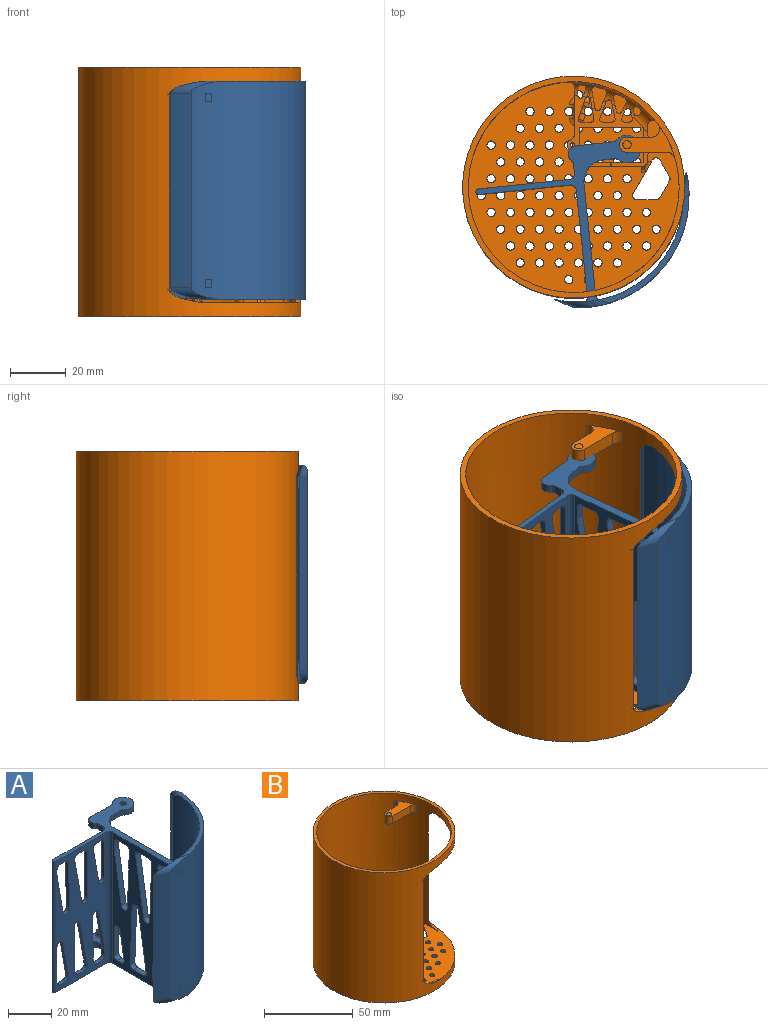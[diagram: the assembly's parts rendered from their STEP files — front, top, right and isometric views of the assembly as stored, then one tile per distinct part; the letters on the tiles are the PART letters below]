
ASSEMBLY  parts=2 mates=1
PART A: 156 faces, bbox 83.3x64.7x78.8 mm
  f0: plane 74x38.02mm, normal (0,1,0), area 1722.9mm2, adj f2,f21,f48,f49,f51,f52,f95,f96
  f1: plane 74x33.02mm, normal (0,-1,0), area 1444.8mm2, adj f21,f48,f95,f96,f97,f98,f99,f100
  f2: plane 71.03x47.74mm, normal (1,0,0), area 1771.1mm2, adj f0,f5,f8,f11,f21,f27,f31,f32
  f3: plane 1.92x1.73mm, normal (0,0,-1), area 0.7mm2, adj f4,f6,f7,f50
  f4: plane 74.05x38.91mm, normal (-1,0,0), area 1618.2mm2, adj f3,f6,f21,f26,f47,f49,f55,f56
  f5: cylinder r=1.5mm len=5.96mm, axis (0,0,-1), area 12.6mm2, adj f2,f7,f50,f140
  f6: cylinder r=1.5mm len=8.91mm, axis (0,0,-1), area 19.4mm2, adj f3,f4,f7,f140
  f7: cylinder r=38mm len=78.8mm, axis (0,0,-1), area 5694.5mm2, adj f3,f5,f6,f13,f14,f15,f16,f17
  f8: plane 26.14x16mm, normal (0,0,-1), area 184.2mm2, adj f2,f9,f33,f34,f35,f36,f37,f38
  f9: plane 4x3.44mm, normal (-1,0,0), area 11.3mm2, adj f8,f32,f38,f52,f135
  f10: plane 4x3.44mm, normal (-1,0,0), area 11.3mm2, adj f11,f21,f29,f51,f137
  f11: plane 26.14x16mm, normal (0,0,-1), area 161.7mm2, adj f2,f10,f22,f23,f24,f25,f28,f29
  f12: cylinder r=40mm len=78.8mm, axis (0,0,-1), area 5675.7mm2, adj f13,f14,f15,f16,f17,f18,f19,f20
  f13: cylinder r=60.11mm len=70mm, axis (0,0,-1), area 551.9mm2, adj f7,f12,f17,f20
  f14: cylinder r=23.1mm len=70mm, axis (0,0,-1), area 236.9mm2, adj f7,f12,f16,f19
  f15: plane 37.31x36.38mm, normal (0,0,-1), area 104mm2, adj f7,f12,f16,f17
  f16: torus R=27.5mm, axis (0,0,-1), area 22.4mm2, adj f7,f12,f14,f15
  f17: torus R=55.71mm, axis (0,0,-1), area 45.8mm2, adj f7,f12,f13,f15
  f18: plane 37.31x36.38mm, normal (0,0,1), area 104mm2, adj f7,f12,f19,f20
  f19: torus R=27.5mm, axis (0,0,1), area 22.4mm2, adj f7,f12,f14,f18
  f20: torus R=55.71mm, axis (0,0,1), area 45.8mm2, adj f7,f12,f13,f18
  f21: plane 60.67x56.26mm, normal (0,0,1), area 398.5mm2, adj f0,f1,f2,f4,f10,f22,f23,f24
  f22: cylinder r=3mm len=5.24mm, axis (0,0,1), area 21.7mm2, adj f11,f21,f25,f29
  f23: plane 3.95x3mm, normal (0,-1,0), area 11.9mm2, adj f11,f21,f30,f31
  f24: cylinder r=5mm len=10mm, axis (0,0,1), area 71.3mm2, adj f11,f21,f28,f30
  f25: plane 13.45x3mm, normal (0,1,0), area 40.4mm2, adj f11,f21,f22,f28
  f26: cylinder r=1.5mm len=6.95mm, axis (0,0,-1), area 12.2mm2, adj f4,f7,f139,f141
  f27: cylinder r=1.5mm len=6.97mm, axis (0,0,-1), area 12.6mm2, adj f2,f7,f139,f141
  f28: cylinder r=1.5mm len=3mm, axis (0,0,1), area 3.6mm2, adj f11,f21,f24,f25
  f29: cylinder r=1.5mm len=3mm, axis (0,0,1), area 3.8mm2, adj f10,f11,f21,f22
  f30: cylinder r=1.5mm len=3mm, axis (0,0,1), area 3.6mm2, adj f11,f21,f23,f24
  f31: cylinder r=8mm len=8mm, axis (0,0,-1), area 37.7mm2, adj f2,f11,f21,f23
  f32: plane 26.14x16mm, normal (0,0,1), area 148.9mm2, adj f2,f9,f33,f34,f35,f36,f37,f38
  f33: cylinder r=3mm len=5.24mm, axis (0,0,-1), area 21.7mm2, adj f8,f32,f34,f38
  f34: plane 13.45x3mm, normal (0,1,0), area 40.4mm2, adj f8,f32,f33,f37
  f35: cylinder r=5mm len=10mm, axis (0,0,-1), area 71.3mm2, adj f8,f32,f37,f39
  f36: plane 3.95x3mm, normal (0,-1,0), area 11.9mm2, adj f8,f32,f39,f40
  f37: cylinder r=1.5mm len=3mm, axis (0,0,-1), area 3.6mm2, adj f8,f32,f34,f35
  f38: cylinder r=1.5mm len=3mm, axis (0,0,-1), area 3.8mm2, adj f8,f9,f32,f33
  f39: cylinder r=1.5mm len=3mm, axis (0,0,-1), area 3.6mm2, adj f8,f32,f35,f36
  f40: cylinder r=8mm len=8mm, axis (0,0,1), area 37.7mm2, adj f2,f8,f32,f36
  f41: cylinder r=1.5mm len=3mm, axis (0,0,-1), area 6.6mm2, adj f21,f42
  f42: plane 6x6mm, normal (0,0,-1), area 21.2mm2, adj f41,f43
  f43: cylinder r=3mm len=6mm, axis (0,0,-1), area 43.4mm2, adj f11,f42
  f44: cylinder r=1.5mm len=3mm, axis (0,0,1), area 6.6mm2, adj f8,f45
  f45: plane 6x6mm, normal (0,0,1), area 21.2mm2, adj f44,f46
  f46: cylinder r=3mm len=6mm, axis (0,0,1), area 43.4mm2, adj f32,f45
  f47: plane 62.05x3mm, normal (0.06,-1,0), area 186.4mm2, adj f2,f4,f139,f140
  f48: plane 36.02x4mm, normal (0,0,-1), area 72.5mm2, adj f0,f1,f49,f138,f155
  f49: cylinder r=3mm len=43mm, axis (0,1,0), area 201.5mm2, adj f0,f2,f4,f48,f50,f60,f66,f74
  f50: torus R=4.5mm, axis (0,0,-1), area 11.1mm2, adj f3,f5,f7,f49
  f51: cylinder r=5mm len=5mm, axis (1,0,0), area 28.2mm2, adj f0,f2,f10,f11,f137
  f52: cylinder r=5mm len=5mm, axis (1,0,0), area 28.2mm2, adj f0,f2,f9,f32,f135
  f53: cylinder r=40mm len=3mm, axis (0,0,-1), area 6.8mm2, adj f12
  f54: cylinder r=40mm len=3mm, axis (0,0,-1), area 6.8mm2, adj f12
  f55: plane 33.19x5.29mm, normal (0,0.99,-0.16), area 100.8mm2, adj f2,f4,f57,f58
  f56: plane 33.19x3mm, normal (0,-1,-0.04), area 99.6mm2, adj f2,f4,f57,f59
  f57: cylinder r=2mm len=3.97mm, axis (1,0,0), area 17.7mm2, adj f2,f4,f55,f56
  f58: cylinder r=2mm len=3mm, axis (1,0,0), area 10.4mm2, adj f2,f4,f55,f60
  f59: cylinder r=2mm len=3mm, axis (-1,0,0), area 9.6mm2, adj f2,f4,f56,f60
  f60: plane 6.53x3mm, normal (0,0,1), area 19.6mm2, adj f4,f49,f58,f59
  f61: plane 15.36x3mm, normal (0,0.99,-0.16), area 46.7mm2, adj f2,f4,f63,f64
  f62: plane 15.36x3mm, normal (0,-1,0), area 46.1mm2, adj f2,f4,f63,f65
  f63: cylinder r=2mm len=3.98mm, axis (-1,0,0), area 17.9mm2, adj f2,f4,f61,f62
  f64: cylinder r=2mm len=3mm, axis (1,0,0), area 10.4mm2, adj f2,f4,f61,f66
  f65: cylinder r=2mm len=3mm, axis (-1,0,0), area 9.4mm2, adj f2,f4,f62,f66
  f66: plane 3x2.45mm, normal (0,0,1), area 7.3mm2, adj f4,f49,f64,f65
  f67: plane 4.14x3mm, normal (0,1,0), area 12.4mm2, adj f2,f4,f70,f73
  f68: plane 29.05x4.63mm, normal (0,0.99,-0.16), area 88.3mm2, adj f2,f4,f70,f71
  f69: plane 33.19x3mm, normal (0,-1,-0.04), area 99.6mm2, adj f2,f4,f71,f72
  f70: cylinder r=2mm len=3mm, axis (1,0,0), area 0.9mm2, adj f2,f4,f67,f68
  f71: cylinder r=2mm len=3.97mm, axis (1,0,0), area 17.7mm2, adj f2,f4,f68,f69
  f72: cylinder r=2mm len=3mm, axis (-1,0,0), area 9.6mm2, adj f2,f4,f69,f74
  f73: cylinder r=2mm len=3mm, axis (1,0,0), area 9.4mm2, adj f2,f4,f67,f74
  f74: plane 5.87x3mm, normal (0,0,1), area 17.6mm2, adj f4,f49,f72,f73
  f75: plane 15.36x3mm, normal (0,-0.99,0.16), area 46.7mm2, adj f2,f4,f78,f79
  f76: plane 3x2.45mm, normal (0,0,-1), area 7.3mm2, adj f2,f4,f79,f80
  f77: plane 15.36x3mm, normal (0,1,0), area 46.1mm2, adj f2,f4,f78,f80
  f78: cylinder r=2mm len=3.98mm, axis (-1,0,0), area 17.9mm2, adj f2,f4,f75,f77
  f79: cylinder r=2mm len=3mm, axis (1,0,0), area 10.4mm2, adj f2,f4,f75,f76
  f80: cylinder r=2mm len=3mm, axis (-1,0,0), area 9.4mm2, adj f2,f4,f76,f77
  f81: plane 33.19x5.29mm, normal (0,-0.99,0.16), area 100.8mm2, adj f2,f4,f84,f86
  f82: plane 33.19x3mm, normal (0,1,0.04), area 99.6mm2, adj f2,f4,f85,f86
  f83: plane 6.53x3mm, normal (0,0,-1), area 19.6mm2, adj f2,f4,f84,f85
  f84: cylinder r=2mm len=3mm, axis (1,0,0), area 10.4mm2, adj f2,f4,f81,f83
  f85: cylinder r=2mm len=3mm, axis (-1,0,0), area 9.6mm2, adj f2,f4,f82,f83
  f86: cylinder r=2mm len=3.97mm, axis (1,0,0), area 17.7mm2, adj f2,f4,f81,f82
  f87: plane 29.05x4.63mm, normal (0,-0.99,0.16), area 88.3mm2, adj f2,f4,f91,f94
  f88: plane 33.19x3mm, normal (0,1,0.04), area 99.6mm2, adj f2,f4,f92,f94
  f89: plane 5.87x3mm, normal (0,0,-1), area 17.6mm2, adj f2,f4,f92,f93
  f90: plane 4.14x3mm, normal (0,-1,0), area 12.4mm2, adj f2,f4,f91,f93
  f91: cylinder r=2mm len=3mm, axis (1,0,0), area 0.9mm2, adj f2,f4,f87,f90
  f92: cylinder r=2mm len=3mm, axis (-1,0,0), area 9.6mm2, adj f2,f4,f88,f89
  f93: cylinder r=2mm len=3mm, axis (1,0,0), area 9.4mm2, adj f2,f4,f89,f90
  f94: cylinder r=2mm len=3.97mm, axis (1,0,0), area 17.7mm2, adj f2,f4,f87,f88
  f95: plane 25.99x4.58mm, normal (-0.98,0,-0.17), area 52.8mm2, adj f0,f1,f98,f100
  f96: plane 25.99x2mm, normal (1,0,0.01), area 52mm2, adj f0,f1,f99,f100
  f97: plane 4.26x2mm, normal (0,0,1), area 8.5mm2, adj f0,f1,f98,f99
  f98: cylinder r=2mm len=2.35mm, axis (0,1,0), area 7mm2, adj f0,f1,f95,f97
  f99: cylinder r=2mm len=2mm, axis (0,-1,0), area 6.2mm2, adj f0,f1,f96,f97
  f100: cylinder r=2mm len=3.97mm, axis (0,1,0), area 11.9mm2, adj f0,f1,f95,f96
  f101: plane 20.47x3.61mm, normal (0.98,0,0.17), area 41.6mm2, adj f0,f1,f104,f105
  f102: plane 3.61x2mm, normal (0,0,-1), area 7.2mm2, adj f0,f1,f105,f106
  f103: plane 20.46x2mm, normal (-1,0,0), area 40.9mm2, adj f0,f1,f104,f106
  f104: cylinder r=2mm len=3.97mm, axis (0,-1,0), area 11.9mm2, adj f0,f1,f101,f103
  f105: cylinder r=2mm len=2.35mm, axis (0,1,0), area 7mm2, adj f0,f1,f101,f102
  f106: cylinder r=2mm len=2mm, axis (0,-1,0), area 6.3mm2, adj f0,f1,f102,f103
  f107: plane 25.99x4.58mm, normal (0.98,0,0.17), area 52.8mm2, adj f0,f1,f110,f112
  f108: plane 25.99x2mm, normal (-1,0,-0.01), area 52mm2, adj f0,f1,f111,f112
  f109: plane 4.26x2mm, normal (0,0,-1), area 8.5mm2, adj f0,f1,f110,f111
  f110: cylinder r=2mm len=2.35mm, axis (0,1,0), area 7mm2, adj f0,f1,f107,f109
  f111: cylinder r=2mm len=2mm, axis (0,-1,0), area 6.2mm2, adj f0,f1,f108,f109
  f112: cylinder r=2mm len=3.97mm, axis (0,1,0), area 11.9mm2, adj f0,f1,f107,f108
  f113: plane 20.47x3.61mm, normal (-0.98,0,-0.17), area 41.6mm2, adj f0,f1,f116,f117
  f114: plane 3.61x2mm, normal (0,0,1), area 7.2mm2, adj f0,f1,f117,f118
  f115: plane 20.46x2mm, normal (1,0,0), area 40.9mm2, adj f0,f1,f116,f118
  f116: cylinder r=2mm len=3.97mm, axis (0,-1,0), area 11.9mm2, adj f0,f1,f113,f115
  f117: cylinder r=2mm len=2.35mm, axis (0,1,0), area 7mm2, adj f0,f1,f113,f114
  f118: cylinder r=2mm len=2mm, axis (0,1,0), area 6.3mm2, adj f0,f1,f114,f115
  f119: plane 25.99x2mm, normal (-1,0,-0.01), area 52mm2, adj f0,f1,f124,f126
  f120: plane 22.78x4.02mm, normal (0.98,0,0.17), area 46.3mm2, adj f0,f1,f123,f126
  f121: plane 3.7x2mm, normal (0,0,-1), area 7.4mm2, adj f0,f1,f124,f125
  f122: plane 3.21x2mm, normal (1,0,0), area 6.4mm2, adj f0,f1,f123,f125
  f123: cylinder r=2mm len=2mm, axis (0,1,0), area 0.7mm2, adj f0,f1,f120,f122
  f124: cylinder r=2mm len=2mm, axis (0,-1,0), area 6.2mm2, adj f0,f1,f119,f121
  f125: cylinder r=2mm len=2mm, axis (0,-1,0), area 6.3mm2, adj f0,f1,f121,f122
  f126: cylinder r=2mm len=3.97mm, axis (0,1,0), area 11.9mm2, adj f0,f1,f119,f120
  f127: plane 3.7x2mm, normal (0,0,1), area 7.4mm2, adj f0,f1,f131,f133
  f128: plane 3.21x2mm, normal (-1,0,0), area 6.4mm2, adj f0,f1,f132,f133
  f129: plane 22.78x4.02mm, normal (-0.98,0,-0.17), area 46.3mm2, adj f0,f1,f132,f134
  f130: plane 25.99x2mm, normal (1,0,0.01), area 52mm2, adj f0,f1,f131,f134
  f131: cylinder r=2mm len=2mm, axis (0,-1,0), area 6.2mm2, adj f0,f1,f127,f130
  f132: cylinder r=2mm len=2mm, axis (0,1,0), area 0.7mm2, adj f0,f1,f128,f129
  f133: cylinder r=2mm len=2mm, axis (0,1,0), area 6.3mm2, adj f0,f1,f127,f128
  f134: cylinder r=2mm len=3.97mm, axis (0,1,0), area 11.9mm2, adj f0,f1,f129,f130
  f135: cylinder r=2mm len=10mm, axis (0,0,-1), area 22mm2, adj f0,f9,f52,f136
  f136: cylinder r=2mm len=5mm, axis (-1,0,0), area 12.5mm2, adj f0,f2,f8,f49,f135
  f137: cylinder r=2mm len=8mm, axis (0,0,-1), area 18.8mm2, adj f0,f10,f21,f51
  f138: cylinder r=2mm len=74mm, axis (0,0,1), area 232.5mm2, adj f1,f4,f21,f48
  f139: bspline ~6.4x1.97mm, area 12.7mm2, adj f7,f26,f27,f47
  f140: bspline ~6.25x1.97mm, area 12.7mm2, adj f5,f6,f7,f47
  f141: torus R=36mm, axis (0,0,1), area 12.8mm2, adj f2,f4,f7,f21,f26,f27
  f142: cylinder r=0.7mm len=3mm, axis (0,0,1), area 13.2mm2, adj f8,f32
  f143: cylinder r=0.7mm len=3mm, axis (0,0,1), area 13.2mm2, adj f8,f32
  f144: cylinder r=0.7mm len=3mm, axis (0,0,1), area 13.2mm2, adj f8,f32
  f145: cylinder r=0.7mm len=3mm, axis (0,0,1), area 13.2mm2, adj f8,f32
  f146: cylinder r=0.7mm len=3mm, axis (0,0,1), area 13.2mm2, adj f8,f32
  f147: cylinder r=2.28mm len=4.54mm, axis (0,0,-1), area 9.9mm2, adj f148,f150,f151,f152,f153,f154
  f148: plane 1.5x0.7mm, normal (1,-0.08,0), area 0.4mm2, adj f32,f147,f149,f152,f153
  f149: cylinder r=2.08mm len=4.15mm, axis (0,0,-1), area 12.1mm2, adj f32,f148,f150,f151,f153,f154
  f150: plane 1.5x0.7mm, normal (1,0.08,0), area 0.4mm2, adj f32,f147,f149,f152,f154
  f151: plane 4.35x1.61mm, normal (0,0,1), area 1.1mm2, adj f147,f149,f153,f154
  f152: torus R=2.78mm, axis (0,0,-1), area 5.8mm2, adj f32,f147,f148,f150
  f153: cylinder r=0.5mm len=0.52mm, axis (-0.08,-1,0), area 0.2mm2, adj f147,f148,f149,f151
  f154: cylinder r=0.5mm len=0.52mm, axis (0.08,-1,0), area 0.2mm2, adj f147,f149,f150,f151
  f155: cylinder r=1mm len=74mm, axis (0,0,-1), area 232.5mm2, adj f0,f1,f21,f48
PART B: 219 faces, bbox 89.8x86x90.2 mm
  f0: bspline ~2x1.98mm, area 1.2mm2, adj f66,f197,f203,f205
  f1: plane 4.54x3.28mm, normal (0,0,-1), area 5.9mm2, adj f118,f133,f136,f162,f166,f179,f195,f196
  f2: plane 8.23x1.5mm, normal (0,0,-1), area 12.3mm2, adj f5,f6,f187,f200
  f3: plane 76x76mm, normal (0,0,-1), area 3835.2mm2, adj f8,f9,f10,f11,f12,f13,f14,f15
  f4: plane 31.67x25.08mm, normal (0,0,-1), area 152.4mm2, adj f118,f119,f120,f121,f123,f124,f125,f126
  f5: plane 10.93x6.7mm, normal (0,-1,0), area 45.3mm2, adj f2,f7,f131,f187,f200
  f6: plane 20.8x11.43mm, normal (0,1,0), area 55.7mm2, adj f2,f7,f99,f126,f187,f194,f200
  f7: plane 31.67x25.53mm, normal (0,0,1), area 196.3mm2, adj f5,f6,f118,f119,f120,f121,f122,f123
  f8: cylinder r=1.5mm len=3mm, axis (0,0,-1), area 9.4mm2, adj f3,f99
  f9: cylinder r=1.5mm len=3mm, axis (0,0,-1), area 9.4mm2, adj f3,f99
  f10: cylinder r=1.5mm len=3mm, axis (0,0,-1), area 9.4mm2, adj f3,f99
  f11: cylinder r=1.5mm len=3mm, axis (0,0,-1), area 9.4mm2, adj f3,f99
  f12: cylinder r=1.5mm len=3mm, axis (0,0,-1), area 9.4mm2, adj f3,f99
  f13: cylinder r=1.5mm len=3mm, axis (0,0,-1), area 9.4mm2, adj f3,f99
  f14: cylinder r=1.5mm len=3mm, axis (0,0,-1), area 9.4mm2, adj f3,f99
  f15: cylinder r=1.5mm len=3mm, axis (0,0,-1), area 9.4mm2, adj f3,f99
  f16: cylinder r=1.5mm len=3mm, axis (0,0,-1), area 9.4mm2, adj f3,f99
  f17: cylinder r=1.5mm len=3mm, axis (0,0,-1), area 9.4mm2, adj f3,f99
  f18: cylinder r=1.5mm len=3mm, axis (0,0,-1), area 9.4mm2, adj f3,f99
  f19: cylinder r=1.5mm len=3mm, axis (0,0,-1), area 9.4mm2, adj f3,f99
  f20: cylinder r=1.5mm len=3mm, axis (0,0,-1), area 9.4mm2, adj f3,f99
  f21: cylinder r=1.5mm len=3mm, axis (0,0,-1), area 9.4mm2, adj f3,f99
  f22: cylinder r=1.5mm len=3mm, axis (0,0,-1), area 9.4mm2, adj f3,f99
  f23: cylinder r=1.5mm len=3mm, axis (0,0,-1), area 9.4mm2, adj f3,f99
  f24: cylinder r=1.5mm len=3mm, axis (0,0,-1), area 9.4mm2, adj f3,f99
  f25: cylinder r=1.5mm len=3mm, axis (0,0,-1), area 9.4mm2, adj f3,f99
  f26: cylinder r=1.5mm len=3mm, axis (0,0,-1), area 9.4mm2, adj f3,f99
  f27: cylinder r=1.5mm len=3mm, axis (0,0,-1), area 9.4mm2, adj f3,f99
  f28: cylinder r=1.5mm len=3mm, axis (0,0,-1), area 9.4mm2, adj f3,f99
  f29: cylinder r=1.5mm len=3mm, axis (0,0,-1), area 9.4mm2, adj f3,f99
  f30: cylinder r=1.5mm len=3mm, axis (0,0,-1), area 9.4mm2, adj f3,f99
  f31: cylinder r=1.5mm len=3mm, axis (0,0,-1), area 9.4mm2, adj f3,f99
  f32: cylinder r=1.5mm len=3mm, axis (0,0,-1), area 9.4mm2, adj f3,f99
  f33: cylinder r=1.5mm len=3mm, axis (0,0,-1), area 9.4mm2, adj f3,f99
  f34: cylinder r=1.5mm len=3mm, axis (0,0,-1), area 9.4mm2, adj f3,f99
  f35: cylinder r=1.5mm len=3mm, axis (0,0,-1), area 9.4mm2, adj f3,f99
  f36: cylinder r=1.5mm len=3mm, axis (0,0,-1), area 9.4mm2, adj f3,f99
  f37: cylinder r=1.5mm len=3mm, axis (0,0,-1), area 9.4mm2, adj f3,f99
  f38: cylinder r=1.5mm len=3mm, axis (0,0,-1), area 9.4mm2, adj f3,f99
  f39: cylinder r=1.5mm len=3mm, axis (0,0,-1), area 9.4mm2, adj f3,f99
  f40: cylinder r=1.5mm len=3mm, axis (0,0,-1), area 9.4mm2, adj f3,f99
  f41: cylinder r=1.5mm len=3mm, axis (0,0,-1), area 9.4mm2, adj f3,f99
  f42: cylinder r=1.5mm len=3mm, axis (0,0,-1), area 9.4mm2, adj f3,f99
  f43: cylinder r=1.5mm len=3mm, axis (0,0,-1), area 9.4mm2, adj f3,f99
  f44: cylinder r=1.5mm len=3mm, axis (0,0,-1), area 9.4mm2, adj f3,f99
  f45: cylinder r=1.5mm len=3mm, axis (0,0,-1), area 9.4mm2, adj f3,f99
  f46: cylinder r=1.5mm len=3mm, axis (0,0,-1), area 9.4mm2, adj f3,f99
  f47: cylinder r=1.5mm len=3mm, axis (0,0,-1), area 9.4mm2, adj f3,f99
  f48: cylinder r=1.5mm len=3mm, axis (0,0,-1), area 9.4mm2, adj f3,f99
  f49: cylinder r=1.5mm len=3mm, axis (0,0,-1), area 9.4mm2, adj f3,f99
  f50: cylinder r=1.5mm len=3mm, axis (0,0,-1), area 9.4mm2, adj f3,f99
  f51: cylinder r=1.5mm len=3mm, axis (0,0,-1), area 9.4mm2, adj f3,f99
  f52: cylinder r=1.5mm len=3mm, axis (0,0,-1), area 9.4mm2, adj f3,f99
  f53: cylinder r=1.5mm len=3mm, axis (0,0,-1), area 9.4mm2, adj f3,f99
  f54: cylinder r=1.5mm len=3mm, axis (0,0,-1), area 9.4mm2, adj f3,f99
  f55: cylinder r=1.5mm len=3mm, axis (0,0,-1), area 9.4mm2, adj f3,f99
  f56: cylinder r=1.5mm len=3mm, axis (0,0,-1), area 9.4mm2, adj f3,f99
  f57: cylinder r=1.5mm len=3mm, axis (0,0,-1), area 9.4mm2, adj f3,f99
  f58: cylinder r=1.5mm len=3mm, axis (0,0,-1), area 9.4mm2, adj f3,f99
  f59: cylinder r=1.5mm len=3mm, axis (0,0,-1), area 9.4mm2, adj f3,f99
  f60: cylinder r=1.5mm len=3mm, axis (0,0,-1), area 9.4mm2, adj f3,f99
  f61: cylinder r=1.5mm len=3mm, axis (0,0,-1), area 9.4mm2, adj f3,f99
  f62: cylinder r=1.5mm len=3mm, axis (0,0,-1), area 9.4mm2, adj f3,f99
  f63: cylinder r=1.5mm len=3mm, axis (0,0,-1), area 9.4mm2, adj f3,f99
  f64: cylinder r=1.5mm len=3mm, axis (0,0,-1), area 9.4mm2, adj f3,f99
  f65: cylinder r=1.5mm len=3mm, axis (0,0,-1), area 9.4mm2, adj f3,f99,f209
  f66: cylinder r=1.5mm len=3mm, axis (0,0,-1), area 9.4mm2, adj f0,f3,f99,f203
  f67: cylinder r=1.5mm len=3mm, axis (0,0,-1), area 9.4mm2, adj f3,f99
  f68: cylinder r=1.5mm len=3mm, axis (0,0,-1), area 9.4mm2, adj f3,f99
  f69: cylinder r=1.5mm len=3mm, axis (0,0,-1), area 9.4mm2, adj f3,f99
  f70: cylinder r=1.5mm len=3mm, axis (0,0,-1), area 9.4mm2, adj f3,f99
  f71: cylinder r=1.5mm len=3mm, axis (0,0,-1), area 9.4mm2, adj f3,f99
  f72: cylinder r=1.5mm len=3mm, axis (0,0,-1), area 9.4mm2, adj f3,f99
  f73: cylinder r=1.5mm len=3mm, axis (0,0,-1), area 9.4mm2, adj f3,f99
  f74: cylinder r=1.5mm len=3mm, axis (0,0,-1), area 10.1mm2, adj f3,f99,f208,f210
  f75: cylinder r=1.5mm len=3mm, axis (0,0,-1), area 9.4mm2, adj f3,f99,f204
  f76: cylinder r=1.5mm len=3mm, axis (0,0,-1), area 9.4mm2, adj f3,f99
  f77: cylinder r=1.5mm len=3mm, axis (0,0,-1), area 9.4mm2, adj f3,f99
  f78: cylinder r=1.5mm len=3mm, axis (0,0,-1), area 9.4mm2, adj f3,f99
  f79: cylinder r=1.5mm len=3mm, axis (0,0,-1), area 9.4mm2, adj f3,f99
  f80: cylinder r=1.5mm len=2.25mm, axis (0,0,-1), area 3.1mm2, adj f3,f99,f191,f192
  f81: cylinder r=1.5mm len=3mm, axis (0,0,-1), area 9.4mm2, adj f3,f99
  f82: cylinder r=1.5mm len=3mm, axis (0,0,-1), area 9.4mm2, adj f3,f99
  f83: cylinder r=1.5mm len=3mm, axis (0,0,-1), area 9.4mm2, adj f3,f99
  f84: cylinder r=1.5mm len=3mm, axis (0,0,-1), area 9.4mm2, adj f3,f99
  f85: cylinder r=1.5mm len=3mm, axis (0,0,-1), area 9.4mm2, adj f3,f99
  f86: cylinder r=1.5mm len=1.3mm, axis (0,0,-1), area 1.6mm2, adj f3,f99,f190,f191
  f87: cylinder r=1.5mm len=3mm, axis (0,0,-1), area 9.4mm2, adj f3,f99
  f88: cylinder r=1.5mm len=3mm, axis (0,0,-1), area 9.4mm2, adj f3,f99
  f89: cylinder r=1.5mm len=6mm, axis (0,0,-1), area 56.5mm2, adj f3,f106
  f90: cylinder r=1.5mm len=2.6mm, axis (0,0,-1), area 3.1mm2, adj f3,f99,f189,f192
  f91: cylinder r=1.5mm len=1.5mm, axis (0,0,-1), area 1.6mm2, adj f3,f99,f189,f190
  f92: cylinder r=38mm len=76mm, axis (0,0,-1), area 955mm2, adj f3,f96
  f93: cylinder r=38mm len=17.49mm, axis (0,0,-1), area 44.8mm2, adj f94,f99,f101
  f94: cylinder r=38mm len=85mm, axis (0,0,-1), area 13467.1mm2, adj f93,f97,f98,f99,f100,f106,f107,f108
  f95: cylinder r=40mm len=90mm, axis (0,0,-1), area 16607.6mm2, adj f96,f97,f98,f99,f100,f101,f107,f108
  f96: plane 80x80mm, normal (0,0,-1), area 490.1mm2, adj f92,f95
  f97: cylinder r=60.71mm len=70mm, axis (0,0,-1), area 608.9mm2, adj f94,f95,f101,f110
  f98: cylinder r=22.5mm len=70mm, axis (0,0,-1), area 240.3mm2, adj f94,f95,f100,f109
  f99: plane 77.9x77.25mm, normal (0,0,1), area 3789.4mm2, adj f6,f8,f9,f10,f11,f12,f13,f14
  f100: torus R=27.5mm, axis (0,0,-1), area 27.9mm2, adj f94,f95,f98,f99
  f101: torus R=55.71mm, axis (0,0,-1), area 55.3mm2, adj f93,f95,f97,f99
  f102: plane 14.46x5mm, normal (0,-1,0), area 72.3mm2, adj f99,f103,f106,f218
  f103: cylinder r=2.75mm len=5.5mm, axis (0,0,-1), area 43.2mm2, adj f99,f102,f104,f106
  f104: plane 8.77x5mm, normal (0,1,0), area 43.9mm2, adj f99,f103,f106,f217
  f105: cylinder r=1.5mm len=5.5mm, axis (0,0,-1), area 51.8mm2, adj f106,f188
  f106: plane 20.1x12.49mm, normal (0,0,1), area 91.3mm2, adj f89,f94,f102,f103,f104,f105,f217,f218
  f107: plane 80x80mm, normal (0,0,1), area 490.1mm2, adj f94,f95
  f108: plane 37.31x36.38mm, normal (0,0,-1), area 104mm2, adj f94,f95,f109,f110
  f109: torus R=27.5mm, axis (0,0,1), area 27.9mm2, adj f94,f95,f98,f108
  f110: torus R=55.71mm, axis (0,0,1), area 55.3mm2, adj f94,f95,f97,f108
  f111: plane 14.46x5mm, normal (0,-1,0), area 72.3mm2, adj f112,f115,f116,f216
  f112: cylinder r=2.75mm len=5.5mm, axis (0,0,1), area 43.2mm2, adj f111,f113,f115,f116
  f113: plane 8.77x5mm, normal (0,1,0), area 43.9mm2, adj f112,f115,f116,f215
  f114: cylinder r=1.5mm len=5mm, axis (0,0,1), area 47.1mm2, adj f115,f116
  f115: plane 20.1x12.49mm, normal (0,0,-1), area 98.4mm2, adj f94,f111,f112,f113,f114,f215,f216
  f116: plane 20.1x12.49mm, normal (0,0,1), area 98.4mm2, adj f94,f111,f112,f113,f114,f215,f216
  f117: plane 4.42x2.29mm, normal (1,0,0), area 9.5mm2, adj f129,f174,f177,f183
  f118: plane 20.24x16.2mm, normal (-1,0,0), area 138.7mm2, adj f1,f4,f7,f128,f176,f179,f180,f196
  f119: cylinder r=2mm len=4mm, axis (0,0,-1), area 18mm2, adj f4,f7,f180,f181
  f120: plane 4x1.28mm, normal (-1,0,0), area 5.1mm2, adj f4,f7,f130,f181
  f121: plane 10.93x4mm, normal (0,-1,0), area 43.7mm2, adj f4,f7,f130,f186
  f122: plane 6.7x1.31mm, normal (1,0,0), area 6.6mm2, adj f7,f131,f182,f199
  f123: plane 11.43x4mm, normal (0,1,0), area 45.7mm2, adj f4,f7,f124,f186
  f124: plane 12.59x4mm, normal (1,0,0), area 50.4mm2, adj f4,f7,f123,f125
  f125: plane 23.03x4mm, normal (0,-1,0), area 92.1mm2, adj f4,f7,f124,f126
  f126: plane 20.8x12.59mm, normal (-1,0,0), area 60.3mm2, adj f4,f6,f7,f99,f125,f193,f199
  f127: cylinder r=2mm len=4mm, axis (0,0,-1), area 17.8mm2, adj f4,f7,f182,f183
  f128: cylinder r=2mm len=14mm, axis (0,0,-1), area 32.2mm2, adj f94,f118,f176,f179
  f129: cylinder r=2mm len=14mm, axis (0,0,-1), area 45.7mm2, adj f94,f117,f174,f177
  f130: cylinder r=2mm len=4mm, axis (0,0,-1), area 12.6mm2, adj f4,f7,f120,f121
  f131: cylinder r=2mm len=18.82mm, axis (0,0,1), area 59.1mm2, adj f5,f7,f122,f193,f194,f213,f214
  f132: plane 7.07x4mm, normal (-0.99,-0.16,0), area 28.7mm2, adj f4,f7,f136,f137
  f133: plane 19.04x7.26mm, normal (0.94,-0.33,0), area 127.5mm2, adj f1,f4,f7,f135,f136,f197,f198,f202
  f134: plane 4x3.69mm, normal (0,1,0), area 14.8mm2, adj f4,f7,f135,f137
  f135: cylinder r=1mm len=4mm, axis (0,0,-1), area 7.6mm2, adj f4,f7,f133,f134
  f136: cylinder r=1mm len=4mm, axis (0,0,-1), area 10.5mm2, adj f1,f4,f7,f132,f133,f175,f178
  f137: cylinder r=1mm len=4mm, axis (0,0,-1), area 6.9mm2, adj f4,f7,f132,f134
  f138: plane 5.09x1.42mm, normal (0.98,0.19,0), area 6.6mm2, adj f141,f143,f174,f177
  f139: plane 6.14x0.73mm, normal (-0.81,0.59,0), area 5mm2, adj f142,f143,f174,f177
  f140: cylinder r=37mm len=8mm, axis (0,0,1), area 8.5mm2, adj f141,f142,f174,f177
  f141: cylinder r=1mm len=8mm, axis (0,0,1), area 15.9mm2, adj f138,f140,f174,f177
  f142: cylinder r=1mm len=8mm, axis (0,0,1), area 10.6mm2, adj f139,f140,f174,f177
  f143: cylinder r=1mm len=5.02mm, axis (0,0,-1), area 10.9mm2, adj f138,f139,f174,f177
  f144: plane 5.24x4.87mm, normal (0.98,0.2,0), area 21.1mm2, adj f4,f7,f147,f149,f174,f177
  f145: plane 6.18x3.51mm, normal (-0.9,0.43,0), area 17.5mm2, adj f4,f7,f148,f149,f174,f177
  f146: cylinder r=37mm len=8mm, axis (0,0,1), area 24.8mm2, adj f147,f148,f174,f177
  f147: cylinder r=1mm len=8mm, axis (0,0,1), area 14.7mm2, adj f144,f146,f174,f177
  f148: cylinder r=1mm len=8mm, axis (0,0,1), area 10.6mm2, adj f145,f146,f174,f177
  f149: cylinder r=1mm len=4mm, axis (0,0,-1), area 10mm2, adj f4,f7,f144,f145
  f150: plane 5.97x4.08mm, normal (-0.98,-0.2,0), area 24.4mm2, adj f4,f7,f154,f155,f174,f177
  f151: plane 5.97x4mm, normal (0.93,-0.38,0), area 25.8mm2, adj f4,f7,f153,f154,f174,f177
  f152: plane 4x3.67mm, normal (0,1,0), area 14.7mm2, adj f4,f7,f153,f155
  f153: cylinder r=1mm len=4mm, axis (0,0,-1), area 7.8mm2, adj f4,f7,f151,f152
  f154: cylinder r=1mm len=4.08mm, axis (0,0,-1), area 10.3mm2, adj f150,f151,f174,f177
  f155: cylinder r=1mm len=4mm, axis (0,0,-1), area 7.1mm2, adj f4,f7,f150,f152
  f156: plane 4.44x2.93mm, normal (-0.98,-0.19,0), area 12.3mm2, adj f4,f7,f160,f161,f174,f177
  f157: plane 4.07x2.93mm, normal (0.9,-0.43,0), area 13mm2, adj f4,f7,f159,f160,f174,f177
  f158: plane 4x1.98mm, normal (0,1,0), area 7.9mm2, adj f4,f7,f159,f161
  f159: cylinder r=1mm len=4mm, axis (0,0,-1), area 8.1mm2, adj f4,f7,f157,f158
  f160: cylinder r=1mm len=4.44mm, axis (0,0,-1), area 10.6mm2, adj f156,f157,f174,f177
  f161: cylinder r=1mm len=4mm, axis (0,0,-1), area 7.1mm2, adj f4,f7,f156,f158
  f162: plane 5.73x2.74mm, normal (-0.94,0.33,0), area 12.9mm2, adj f1,f7,f165,f166,f176,f179
  f163: plane 5.93x2.77mm, normal (1,0,0), area 12.8mm2, adj f166,f167,f176,f179
  f164: cylinder r=37mm len=8mm, axis (0,0,1), area 7.9mm2, adj f165,f167,f176,f179
  f165: cylinder r=1mm len=8mm, axis (0,0,1), area 12.4mm2, adj f162,f164,f176,f179
  f166: cylinder r=1mm len=4.01mm, axis (0,0,-1), area 11.2mm2, adj f1,f7,f162,f163,f176,f179
  f167: cylinder r=1mm len=8mm, axis (0,0,1), area 11.4mm2, adj f163,f164,f176,f179
  f168: plane 6.67x5.51mm, normal (0.99,0.16,0), area 28.4mm2, adj f4,f7,f171,f173,f174,f177
  f169: plane 5.92x5.76mm, normal (-0.93,0.38,0), area 26.6mm2, adj f4,f7,f172,f173,f174,f177
  f170: cylinder r=37mm len=8mm, axis (0,0,1), area 29.3mm2, adj f171,f172,f174,f177
  f171: cylinder r=1mm len=8mm, axis (0,0,1), area 13.2mm2, adj f168,f170,f174,f177
  f172: cylinder r=1mm len=8mm, axis (0,0,1), area 11.4mm2, adj f169,f170,f174,f177
  f173: cylinder r=1mm len=4mm, axis (0,0,-1), area 10.4mm2, adj f4,f7,f168,f169
  f174: torus R=33mm, axis (0,0,1), area 145.6mm2, adj f7,f94,f117,f129,f138,f139,f140,f141
  f175: bspline ~5.13x5.12mm, area 4.3mm2, adj f94,f136,f174,f176
  f176: torus R=33mm, axis (0,0,1), area 31.9mm2, adj f7,f94,f118,f128,f162,f163,f164,f165
  f177: torus R=33mm, axis (0,0,1), area 145.6mm2, adj f4,f94,f117,f129,f138,f139,f140,f141
  f178: bspline ~5.13x5.12mm, area 4.3mm2, adj f94,f136,f177,f179
  f179: torus R=33mm, axis (0,0,1), area 31.9mm2, adj f1,f94,f118,f128,f162,f163,f164,f165
  f180: cylinder r=3mm len=4mm, axis (0,0,-1), area 13.5mm2, adj f4,f7,f118,f119
  f181: cylinder r=3mm len=4mm, axis (0,0,-1), area 13.5mm2, adj f4,f7,f119,f120
  f182: cylinder r=3mm len=4.39mm, axis (0,0,-1), area 13.6mm2, adj f4,f7,f122,f127,f199
  f183: cylinder r=3mm len=4mm, axis (0,0,-1), area 13.4mm2, adj f4,f7,f117,f127,f174,f177
  f184: cylinder r=0.8mm len=4mm, axis (0,0,-1), area 20.1mm2, adj f4,f7
  f185: cylinder r=0.8mm len=4mm, axis (0,0,-1), area 20.1mm2, adj f4,f7
  f186: plane 4x1.5mm, normal (1,0,0), area 6mm2, adj f4,f7,f121,f123
  f187: plane 4x1.5mm, normal (-1,0,0), area 6mm2, adj f2,f5,f6,f7
  f188: torus R=2mm, axis (0,0,1), area 8.3mm2, adj f3,f105
  f189: plane 6.06x3.5mm, normal (-0.87,-0.5,0), area 7mm2, adj f3,f90,f91,f99
  f190: plane 6.06x3.5mm, normal (-0.87,0.5,0), area 7mm2, adj f3,f86,f91,f99
  f191: plane 7x1mm, normal (0,1,0), area 7mm2, adj f3,f80,f86,f99
  f192: plane 12.3x7.17mm, normal (0.87,-0.5,0), area 14mm2, adj f3,f80,f90,f99,f213
  f193: plane 14.22x3.29mm, normal (0,1,0), area 22mm2, adj f99,f126,f131,f199,f213
  f194: plane 14.1x3.5mm, normal (-1,0,0), area 22mm2, adj f6,f99,f131,f200,f214
  f195: plane 14.8x2.04mm, normal (-0.39,0.92,0), area 32.8mm2, adj f1,f196,f198,f210
  f196: cylinder r=1mm len=14.8mm, axis (0,0,1), area 17.3mm2, adj f1,f118,f195,f212
  f197: cylinder r=0.57mm len=14.85mm, axis (0,0,1), area 23.8mm2, adj f0,f4,f118,f133,f201,f203,f205
  f198: cylinder r=0.5mm len=14.8mm, axis (0,0,1), area 17.1mm2, adj f1,f133,f195,f208
  f199: cylinder r=2.7mm len=2.7mm, axis (-1,0,0), area 6.6mm2, adj f4,f122,f126,f182,f193
  f200: cylinder r=2.7mm len=2.7mm, axis (0,-1,0), area 6.4mm2, adj f2,f5,f6,f194
  f201: torus R=2.57mm, axis (0,0,-1), area 2.8mm2, adj f99,f197,f202,f203
  f202: cylinder r=2mm len=2.89mm, axis (0.33,0.94,0), area 7.4mm2, adj f99,f133,f201,f204
  f203: bspline ~2x1.71mm, area 1.2mm2, adj f0,f66,f197,f201
  f204: bspline ~3.3x2.82mm, area 6.9mm2, adj f75,f133,f202,f206
  f205: torus R=2.57mm, axis (0,0,-1), area 5.8mm2, adj f0,f99,f197,f207
  f206: cylinder r=2mm len=2.36mm, axis (0.33,0.94,0), area 4.4mm2, adj f99,f133,f204,f208
  f207: cylinder r=2mm len=2mm, axis (0,1,0), area 3.2mm2, adj f99,f118,f205,f209
  f208: torus R=2.5mm, axis (0,0,-1), area 8.2mm2, adj f74,f99,f198,f206,f210
  f209: bspline ~2.97x2mm, area 6.7mm2, adj f65,f118,f207,f211
  f210: cylinder r=2mm len=2.82mm, axis (-0.92,-0.39,0), area 5mm2, adj f74,f99,f195,f208,f212
  f211: cylinder r=2mm len=2mm, axis (0,1,0), area 2.7mm2, adj f99,f118,f209,f212
  f212: torus R=3mm, axis (0,0,-1), area 6.3mm2, adj f99,f196,f210,f211
  f213: bspline ~4.21x3.21mm, area 7.5mm2, adj f131,f192,f193,f214
  f214: torus R=4mm, axis (0,0,-1), area 3.4mm2, adj f99,f131,f194,f213
  f215: cylinder r=3mm len=5mm, axis (0,0,-1), area 33.2mm2, adj f94,f113,f115,f116
  f216: cylinder r=3mm len=5mm, axis (0,0,-1), area 19.4mm2, adj f94,f111,f115,f116
  f217: cylinder r=3mm len=5mm, axis (0,0,-1), area 33.2mm2, adj f94,f99,f104,f106
  f218: cylinder r=3mm len=5mm, axis (0,0,-1), area 19.4mm2, adj f94,f99,f102,f106
PLACE A rot(axis=(0,0,1),6deg) t=(1.59,-3.41,-1.4)mm
PLACE B t=(0,0,-2)mm
MATE planar A.f18 <-> B.f108  axis (0,0,1) through (30.01,-25.76,83)mm
